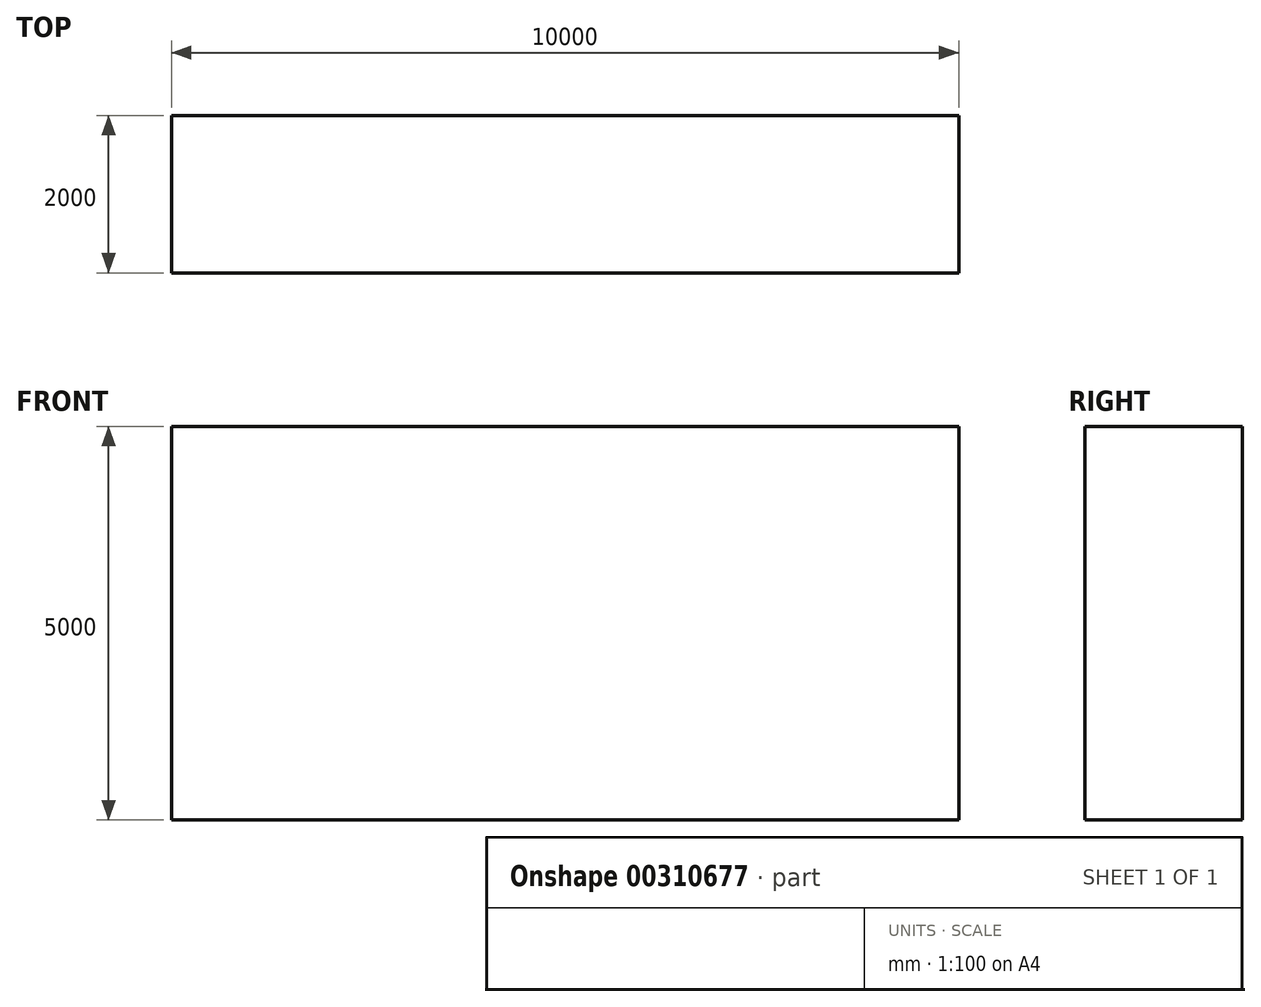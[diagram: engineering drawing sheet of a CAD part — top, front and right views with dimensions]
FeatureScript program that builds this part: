
annotation { "Feature Type Name" : "Feature", "Feature Type Description" : "" }
export const myFeature = defineFeature(function(context is Context, id is Id, definition is map)
    precondition{}
    {
        {
            var Q0;
            Q0=qCreatedBy(makeId("Front.planeOp"),FACE);
            var sketch = newSketch(context, id + "F0", { "sketchPlane" : qUnion([Q0])});
            skLineSegment(sketch, "E0.bottom", {"start": v(0, 0) * mm, "end": v(10000, 0) * mm});
            skLineSegment(sketch, "E0.top", {"start": v(0, -5000) * mm, "end": v(10000, -5000) * mm});
            skLineSegment(sketch, "E0.left", {"start": v(0, 0) * mm, "end": v(0, -5000) * mm});
            skLineSegment(sketch, "E0.right", {"start": v(10000, 0) * mm, "end": v(10000, -5000) * mm});
            skSolve(sketch);
        }
        {
            var Q0;
            Q0=makeQuery(id+"F0.imprint","IMPRINT",FACE,{"disambiguationData":[TD([[makeQuery(id+"F0.imprint","IMPRINT",EDGE,{"derivedFrom":sQuery(id+"F0.wireOp",EDGE,"E0.bottom")}),-1.0]])]});
            extrude(context, id + "F1", {"entities" : qUnion([Q0]), "depth" : 2000 * mm});
        }
    });
